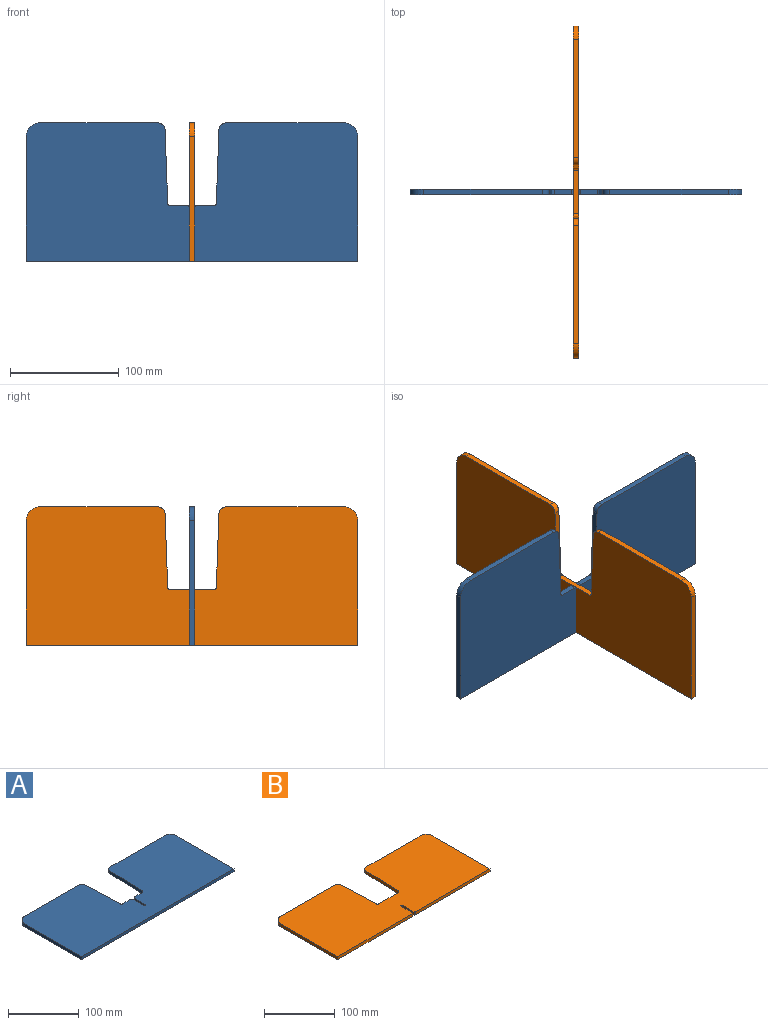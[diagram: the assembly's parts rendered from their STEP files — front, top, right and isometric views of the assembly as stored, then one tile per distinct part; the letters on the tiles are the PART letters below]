
ASSEMBLY  parts=2 mates=1
PART A: 24 faces, bbox 304.8x127x5.1 mm
  f0: plane 108.56x5.08mm, normal (0,1,0), area 551.5mm2, adj f12,f13,f15,f16
  f1: plane 67.64x5.08mm, normal (-1,0.04,0), area 343.8mm2, adj f12,f13,f16,f18
  f2: plane 15.65x5.08mm, normal (0,1,0), area 79.5mm2, adj f12,f13,f18,f19
  f3: plane 22.61x5.08mm, normal (-1,0,0), area 114.8mm2, adj f12,f13,f19,f22
  f4: plane 5.08x2.67mm, normal (0,1,0), area 13.5mm2, adj f12,f13,f22,f23
  f5: plane 22.61x5.08mm, normal (1,0,0), area 114.8mm2, adj f12,f13,f20,f23
  f6: plane 15.65x5.08mm, normal (0,1,0), area 79.5mm2, adj f12,f13,f20,f21
  f7: plane 67.64x5.08mm, normal (1,0.04,0), area 343.8mm2, adj f12,f13,f17,f21
  f8: plane 108.56x5.08mm, normal (0,1,0), area 551.5mm2, adj f12,f13,f14,f17
  f9: plane 114.3x5.08mm, normal (-1,0,0), area 580.6mm2, adj f10,f12,f13,f14
  f10: plane 304.8x5.08mm, normal (0,-1,0), area 1548.4mm2, adj f9,f11,f12,f13
  f11: plane 114.3x5.08mm, normal (1,0,0), area 580.6mm2, adj f10,f12,f13,f15
  f12: plane 304.8x127mm, normal (0,0,1), area 34943.7mm2, adj f0,f1,f2,f3,f4,f5,f6,f7
  f13: plane 304.8x127mm, normal (0,0,-1), area 34943.7mm2, adj f0,f1,f2,f3,f4,f5,f6,f7
  f14: cylinder r=12.7mm len=12.7mm, axis (0,0,-1), area 101.3mm2, adj f8,f9,f12,f13
  f15: cylinder r=12.7mm len=12.7mm, axis (0,0,-1), area 101.3mm2, adj f0,f11,f12,f13
  f16: cylinder r=6.35mm len=6.35mm, axis (0,0,-1), area 49.5mm2, adj f0,f1,f12,f13
  f17: cylinder r=6.35mm len=6.35mm, axis (0,0,-1), area 49.5mm2, adj f7,f8,f12,f13
  f18: cylinder r=2.54mm len=5.08mm, axis (0,0,1), area 19.8mm2, adj f1,f2,f12,f13
  f19: cylinder r=2.54mm len=5.08mm, axis (0,0,-1), area 20.3mm2, adj f2,f3,f12,f13
  f20: cylinder r=2.54mm len=5.08mm, axis (0,0,-1), area 20.3mm2, adj f5,f6,f12,f13
  f21: cylinder r=2.54mm len=5.08mm, axis (0,0,1), area 19.8mm2, adj f6,f7,f12,f13
  f22: cylinder r=0.25mm len=5.08mm, axis (0,0,1), area 2mm2, adj f3,f4,f12,f13
  f23: cylinder r=0.25mm len=5.08mm, axis (0,0,1), area 2mm2, adj f4,f5,f12,f13
PART B: 24 faces, bbox 304.8x127x5.1 mm
  f0: plane 67.64x5.08mm, normal (1,0.04,0), area 343.8mm2, adj f12,f13,f16,f19
  f1: plane 108.56x5.08mm, normal (0,1,0), area 551.5mm2, adj f12,f13,f14,f16
  f2: plane 114.3x5.08mm, normal (-1,0,0), area 580.6mm2, adj f3,f12,f13,f14
  f3: plane 149.54x5.08mm, normal (0,-1,0), area 759.7mm2, adj f2,f12,f13,f22
  f4: plane 23.88x5.08mm, normal (1,0,0), area 121.3mm2, adj f12,f13,f20,f22
  f5: plane 5.08x2.67mm, normal (0,-1,0), area 13.5mm2, adj f12,f13,f20,f21
  f6: plane 23.88x5.08mm, normal (-1,0,0), area 121.3mm2, adj f12,f13,f21,f23
  f7: plane 149.54x5.08mm, normal (0,-1,0), area 759.7mm2, adj f8,f12,f13,f23
  f8: plane 114.3x5.08mm, normal (1,0,0), area 580.6mm2, adj f7,f12,f13,f15
  f9: plane 108.56x5.08mm, normal (0,1,0), area 551.5mm2, adj f12,f13,f15,f17
  f10: plane 67.64x5.08mm, normal (-1,0.04,0), area 343.8mm2, adj f12,f13,f17,f18
  f11: plane 39.55x5.08mm, normal (0,1,0), area 200.9mm2, adj f12,f13,f18,f19
  f12: plane 304.8x127mm, normal (0,0,1), area 34945.7mm2, adj f0,f1,f2,f3,f4,f5,f6,f7
  f13: plane 304.8x127mm, normal (0,0,-1), area 34945.7mm2, adj f0,f1,f2,f3,f4,f5,f6,f7
  f14: cylinder r=12.7mm len=12.7mm, axis (0,0,-1), area 101.3mm2, adj f1,f2,f12,f13
  f15: cylinder r=12.7mm len=12.7mm, axis (0,0,-1), area 101.3mm2, adj f8,f9,f12,f13
  f16: cylinder r=6.35mm len=6.35mm, axis (0,0,-1), area 49.5mm2, adj f0,f1,f12,f13
  f17: cylinder r=6.35mm len=6.35mm, axis (0,0,-1), area 49.5mm2, adj f9,f10,f12,f13
  f18: cylinder r=2.54mm len=5.08mm, axis (0,0,1), area 19.8mm2, adj f10,f11,f12,f13
  f19: cylinder r=2.54mm len=5.08mm, axis (0,0,1), area 19.8mm2, adj f0,f11,f12,f13
  f20: cylinder r=0.25mm len=5.08mm, axis (0,0,1), area 2mm2, adj f4,f5,f12,f13
  f21: cylinder r=0.25mm len=5.08mm, axis (0,0,1), area 2mm2, adj f5,f6,f12,f13
  f22: cylinder r=1.27mm len=5.08mm, axis (0,0,1), area 10.1mm2, adj f3,f4,f12,f13
  f23: cylinder r=1.27mm len=5.08mm, axis (0,0,1), area 10.1mm2, adj f6,f7,f12,f13
PLACE A rot(axis=(1,0,0),90deg) t=(0.25,3.56,-0.51)mm fixed
PLACE B rot(axis=(0.58,0.58,0.58),120deg) t=(150.11,-151.38,-0.51)mm
MATE fastened A.f4 <-> B.f5  axis (0,0,1) through (152.65,1.02,24.89)mm
